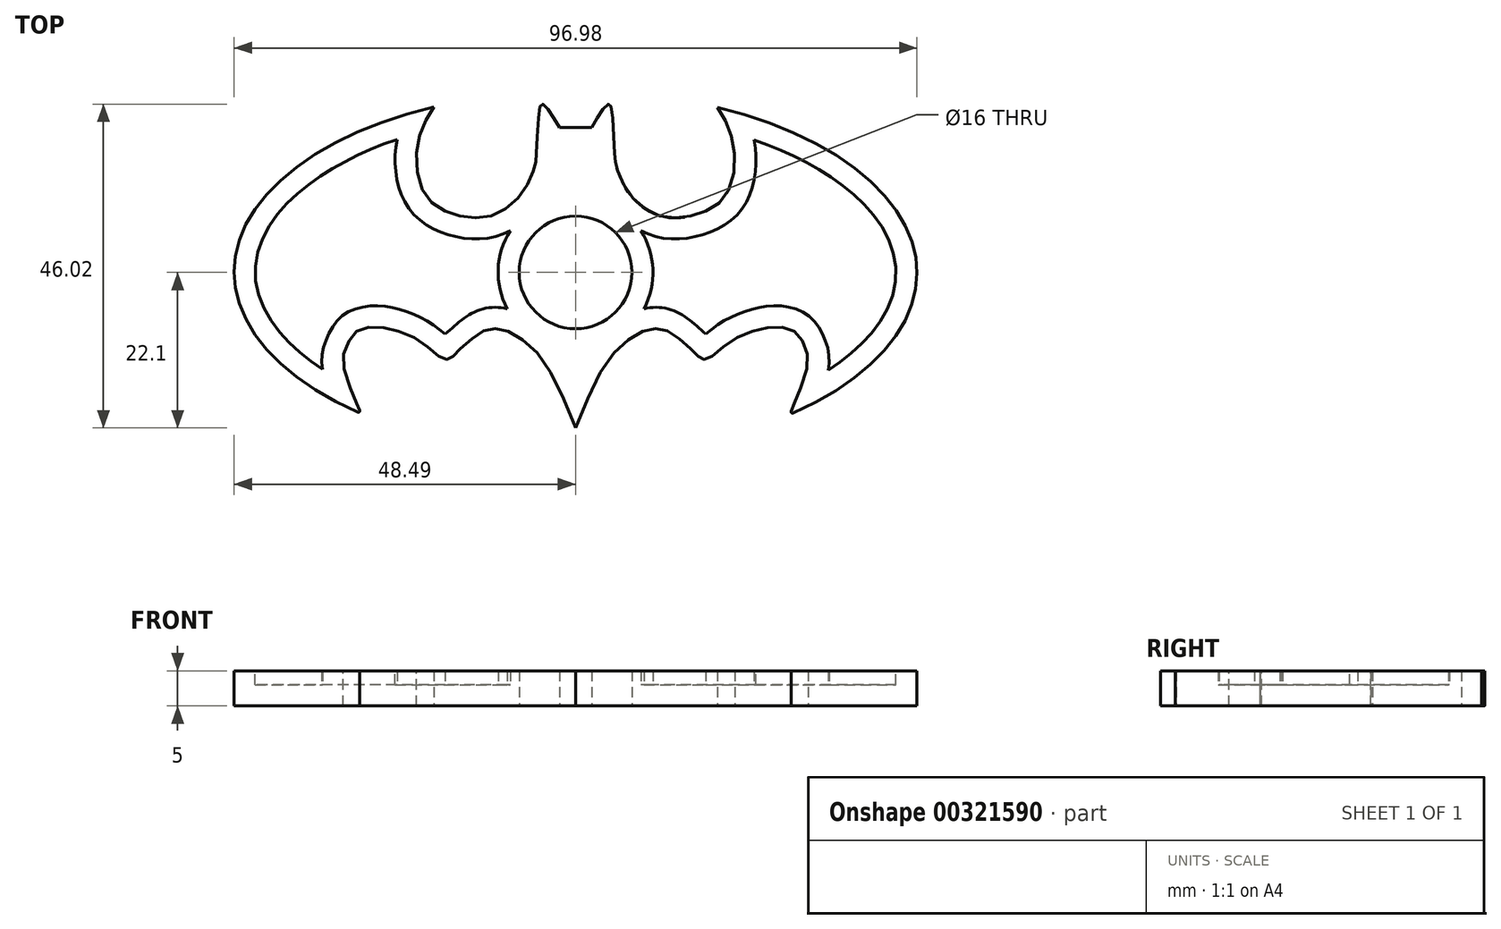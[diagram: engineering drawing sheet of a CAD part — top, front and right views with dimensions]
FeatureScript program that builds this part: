
annotation { "Feature Type Name" : "Feature", "Feature Type Description" : "" }
export const myFeature = defineFeature(function(context is Context, id is Id, definition is map)
    precondition{}
    {
        {
            var Q0;
            Q0=qCreatedBy(makeId("Top.planeOp"),FACE);
            var sketch = newSketch(context, id + "F0", { "sketchPlane" : qUnion([Q0])});
            skFitSpline(sketch, "E0", {"points": [v(-20.13, 25.53) * mm, v(-22.4, 20.3) * mm, v(-21.48, 13.2) * mm, v(-17.16, 10.23) * mm, v(-11.9, 10.06) * mm, v(-7.42, 13.53) * mm, v(-5.72, 17.34) * mm, v(-5.56, 18.65) * mm, v(-5.19, 24.8) * mm, v(-4.86, 25.88) * mm, v(-4.6, 25.88) * mm, v(-3.62, 24.77) * mm, v(-2.28, 22.62) * mm], "startDerivative": vector(-26.09, -43.9) * mm, "endDerivative": vector(18.16, -30.92) * mm});
            skLineSegment(sketch, "E1", {"start": v(-2.28, 22.62) * mm, "end": v(0, 22.62) * mm});
            skFitSpline(sketch, "E2", {"points": [v(0, -20.1) * mm, v(-4.34, -10.9) * mm, v(-7.78, -7.38) * mm, v(-10.33, -6.1) * mm, v(-12.12, -6.03) * mm, v(-13.84, -6.78) * mm, v(-15.94, -8.5) * mm, v(-17.21, -9.7) * mm, v(-17.67, -10.17) * mm, v(-18.2, -10.36) * mm, v(-18.79, -10.28) * mm, v(-20.17, -9.27) * mm, v(-22.6, -7.46) * mm, v(-25.6, -6.23) * mm, v(-28.2, -5.75) * mm, v(-30.53, -6.1) * mm, v(-31.73, -7.02) * mm, v(-32.8, -9.16) * mm, v(-32.93, -11.45) * mm, v(-31.45, -15.7) * mm, v(-30.73, -17.4) * mm], "startDerivative": vector(-40.15, 99.8) * mm, "endDerivative": vector(13.96, -32.46) * mm});
            skPoint(sketch, "E3.first.point", {"position": v(-31.67, -17.2) * mm});
            skPoint(sketch, "E3.second.point", {"position": v(-31.08, -16.59) * mm});
            skPoint(sketch, "E3.third.point", {"position": v(-31.08, -16.59) * mm});
            skLineSegment(sketch, "E4", {"start": v(0, 22.62) * mm, "end": v(0, -25.87) * mm, "construction": true});
            skLineSegment(sketch, "E5.MirrorCS", {"start": v(2.28, 22.62) * mm, "end": v(0, 22.62) * mm});
            skPoint(sketch, "E6.MirrorP", {"position": v(31.08, -16.59) * mm});
            skFitSpline(sketch, "E7.MirrorCS", {"points": [v(0, -20.1) * mm, v(4.34, -10.9) * mm, v(7.78, -7.38) * mm, v(10.33, -6.1) * mm, v(12.12, -6.03) * mm, v(13.84, -6.78) * mm, v(15.94, -8.5) * mm, v(17.21, -9.7) * mm, v(17.67, -10.17) * mm, v(18.2, -10.36) * mm, v(18.79, -10.28) * mm, v(20.17, -9.27) * mm, v(22.6, -7.46) * mm, v(25.6, -6.23) * mm, v(28.2, -5.75) * mm, v(30.53, -6.1) * mm, v(31.73, -7.02) * mm, v(32.8, -9.16) * mm, v(32.93, -11.45) * mm, v(31.45, -15.7) * mm, v(30.73, -17.4) * mm], "startDerivative": vector(40.15, 99.8) * mm, "endDerivative": vector(-13.96, -32.46) * mm});
            skPoint(sketch, "E8.MirrorP", {"position": v(31.67, -17.2) * mm});
            skFitSpline(sketch, "E9.MirrorCS", {"points": [v(20.13, 25.53) * mm, v(22.4, 20.3) * mm, v(21.48, 13.2) * mm, v(17.16, 10.23) * mm, v(11.9, 10.06) * mm, v(7.42, 13.53) * mm, v(5.72, 17.34) * mm, v(5.56, 18.65) * mm, v(5.19, 24.8) * mm, v(4.86, 25.88) * mm, v(4.6, 25.88) * mm, v(3.62, 24.77) * mm, v(2.28, 22.62) * mm], "startDerivative": vector(26.09, -43.9) * mm, "endDerivative": vector(-18.16, -30.92) * mm});
            skCircle(sketch, "E10", {"center": v(0, 2) * mm, "radius": 8 * mm});
            skLineSegment(sketch, "E11", {"start": v(-48.5, 2.1) * mm, "end": v(48.5, 2.1) * mm, "construction": true});
            skEllipticalArc(sketch, "E12", {});
            skLineSegment(sketch, "E13", {"start": v(-31.08, -16.59) * mm, "end": v(-30.65, -17.6) * mm});
            skEllipticalArc(sketch, "E14.trimOffspring", {});
            skPoint(sketch, "E15.visualSharp", {"position": v(-30.45, -18.07) * mm});
            skArc(sketch, "E15.filletArc", {"start": v(-30.91, -17.86) * mm, "mid": v(-30.69, -17.82) * mm, "end": v(-30.65, -17.6) * mm});
            skLineSegment(sketch, "E16", {"start": v(31.08, -16.59) * mm, "end": v(30.61, -17.7) * mm});
            skPoint(sketch, "E17.visualSharp", {"position": v(30.42, -18.16) * mm});
            skArc(sketch, "E17.filletArc", {"start": v(30.61, -17.7) * mm, "mid": v(30.66, -17.93) * mm, "end": v(30.88, -17.97) * mm});
            const initialGuessF0  = {"E12": [0, 0.002, -0.9999979750292427, 0.002012445630099361, 0.048492257889837395, 0.02583750383918345, 5.14158624500311, 0.8807092972419206], "E14.trimOffspring": [0, 0.002, -0.9999979750292427, 0.002012445630099361, 0.048492257889837395, 0.02583750383918345, 2.262116125750283, 4.284421521285877]};
            skSetInitialGuess(sketch, initialGuessF0);
            skSolve(sketch);
        }
        {
            var Q0;
            Q0=qSketchRegion(id+"F0",true);
            extrude(context, id + "F1", {"entities" : qUnion([Q0]), "depth" : 5 * mm});
        }
        {
            var Q0;
            Q0=makeQuery(id+"F1.opExtrude","CAP_FACE",FACE,{"disambiguationData":[OSD([sQuery(id+"F0.wireOp",EDGE,"E0"),sQuery(id+"F0.wireOp",EDGE,"E1"),sQuery(id+"F0.wireOp",EDGE,"E2"),sQuery(id+"F0.wireOp",EDGE,"E5.MirrorCS"),sQuery(id+"F0.wireOp",EDGE,"E7.MirrorCS"),sQuery(id+"F0.wireOp",EDGE,"E9.MirrorCS"),sQuery(id+"F0.wireOp",EDGE,"E10"),sQuery(id+"F0.wireOp",EDGE,"E12"),sQuery(id+"F0.wireOp",EDGE,"E13"),sQuery(id+"F0.wireOp",EDGE,"E14.trimOffspring"),sQuery(id+"F0.wireOp",EDGE,"E15.filletArc"),sQuery(id+"F0.wireOp",EDGE,"E16"),sQuery(id+"F0.wireOp",EDGE,"E17.filletArc")])],"isStart":false});
            shell(context, id + "F2", {"entities" : qUnion([Q0]), "thickness" : 3 * mm});
        }
        {
            var Q0;
            Q0=makeQuery(id+"F1.opExtrude","CAP_FACE",FACE,{"disambiguationData":[OSD([sQuery(id+"F0.wireOp",EDGE,"E0"),sQuery(id+"F0.wireOp",EDGE,"E1"),sQuery(id+"F0.wireOp",EDGE,"E2"),sQuery(id+"F0.wireOp",EDGE,"E5.MirrorCS"),sQuery(id+"F0.wireOp",EDGE,"E7.MirrorCS"),sQuery(id+"F0.wireOp",EDGE,"E9.MirrorCS"),sQuery(id+"F0.wireOp",EDGE,"E10"),sQuery(id+"F0.wireOp",EDGE,"E12"),sQuery(id+"F0.wireOp",EDGE,"E13"),sQuery(id+"F0.wireOp",EDGE,"E14.trimOffspring"),sQuery(id+"F0.wireOp",EDGE,"E15.filletArc"),sQuery(id+"F0.wireOp",EDGE,"E16"),sQuery(id+"F0.wireOp",EDGE,"E17.filletArc")])],"isStart":false});
            var sketch = newSketch(context, id + "F3", { "sketchPlane" : qUnion([Q0])});
            skLineSegment(sketch, "E18", {"start": v(-3.81, 21.13) * mm, "end": v(-7.1, 9.91) * mm});
            skLineSegment(sketch, "E19", {"start": v(-7.1, 9.91) * mm, "end": v(-1.68, 10.88) * mm});
            skLineSegment(sketch, "E20", {"start": v(-1.68, 10.88) * mm, "end": v(3.05, 10.6) * mm});
            skLineSegment(sketch, "E21", {"start": v(3.05, 10.6) * mm, "end": v(6.92, 9.33) * mm});
            skLineSegment(sketch, "E22", {"start": v(6.92, 9.33) * mm, "end": v(5.86, 13.59) * mm});
            skLineSegment(sketch, "E23", {"start": v(5.86, 13.59) * mm, "end": v(4.12, 20.94) * mm});
            skLineSegment(sketch, "E24", {"start": v(4.12, 20.94) * mm, "end": v(-3.81, 21.13) * mm});
            skLineSegment(sketch, "E25", {"start": v(-3.04, -7.49) * mm, "end": v(3.92, -7.59) * mm});
            skLineSegment(sketch, "E26", {"start": v(3.92, -7.59) * mm, "end": v(0.35, -15.22) * mm});
            skLineSegment(sketch, "E27", {"start": v(0.35, -15.22) * mm, "end": v(-3.42, -8.84) * mm});
            skLineSegment(sketch, "E28", {"start": v(-3.42, -8.84) * mm, "end": v(-3.04, -7.49) * mm});
            skSolve(sketch);
        }
        {
            var Q0;
            Q0=qSketchRegion(id+"F3",true);
            var Q1;
            Q1=makeQuery(id+"F2.opShell","OFFSET_FACE",FACE,{"disambiguationData":[OSD([sQuery(id+"F0.wireOp",EDGE,"E0"),sQuery(id+"F0.wireOp",EDGE,"E1"),sQuery(id+"F0.wireOp",EDGE,"E2"),sQuery(id+"F0.wireOp",EDGE,"E5.MirrorCS"),sQuery(id+"F0.wireOp",EDGE,"E7.MirrorCS"),sQuery(id+"F0.wireOp",EDGE,"E9.MirrorCS"),sQuery(id+"F0.wireOp",EDGE,"E10"),sQuery(id+"F0.wireOp",EDGE,"E12"),sQuery(id+"F0.wireOp",EDGE,"E13"),sQuery(id+"F0.wireOp",EDGE,"E14.trimOffspring"),sQuery(id+"F0.wireOp",EDGE,"E15.filletArc"),sQuery(id+"F0.wireOp",EDGE,"E16"),sQuery(id+"F0.wireOp",EDGE,"E17.filletArc")]),OD(2.0)]});
            extrude(context, id + "F4", {"entities" : qUnion([Q0]), "operationType" : NewBodyOperationType.ADD, "oppositeDirection" : true, "endBoundEntityFace" : qUnion([Q1]), "depth" : 4 * mm});
        }
    });
